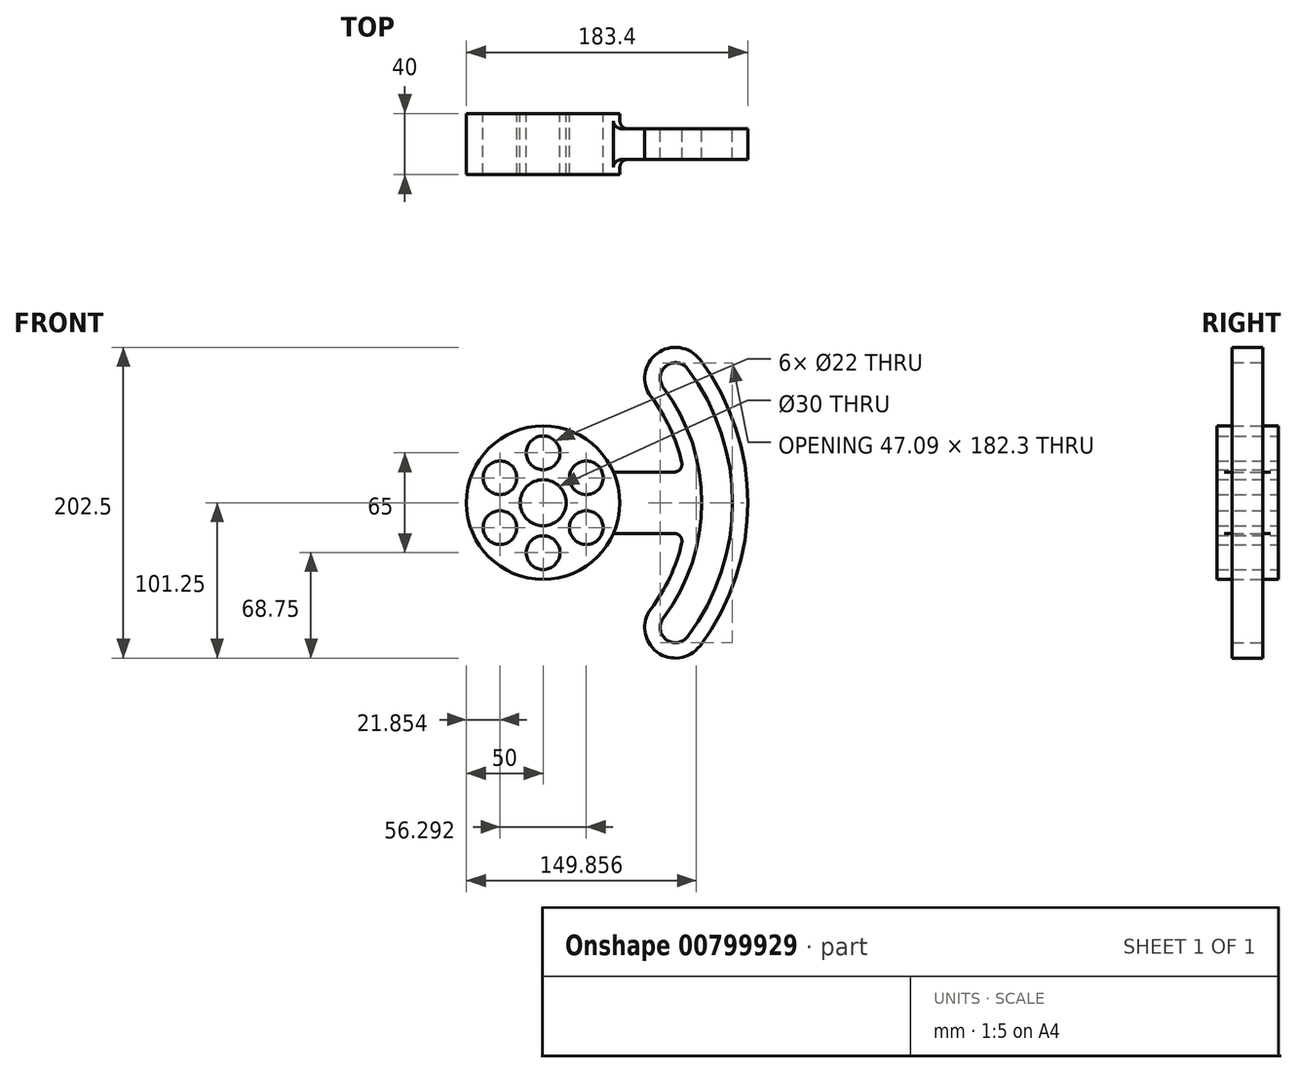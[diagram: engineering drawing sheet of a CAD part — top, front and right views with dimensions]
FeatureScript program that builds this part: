
annotation { "Feature Type Name" : "Feature", "Feature Type Description" : "" }
export const myFeature = defineFeature(function(context is Context, id is Id, definition is map)
    precondition{}
    {
        {
            var Q0;
            Q0=qCreatedBy(makeId("Front.planeOp"),FACE);
            var sketch = newSketch(context, id + "F0", { "sketchPlane" : qUnion([Q0])});
            skCircle(sketch, "E0", {"center": v(0, 0) * mm, "radius": 50 * mm});
            skCircle(sketch, "E1", {"center": v(0, 0) * mm, "radius": 15 * mm});
            skCircle(sketch, "E2", {"center": v(0, 0) * mm, "radius": 32.5 * mm, "construction": true});
            skCircle(sketch, "E3", {"center": v(0, 32.5) * mm, "radius": 11 * mm});
            skPoint(sketch, "E4.center", {"position": v(-21.6, 0) * mm});
            skCircle(sketch, "E5.1.0", {"center": v(-28.15, 16.25) * mm, "radius": 11 * mm});
            skCircle(sketch, "E5.2.0", {"center": v(-28.15, -16.25) * mm, "radius": 11 * mm});
            skCircle(sketch, "E5.3.0", {"center": v(0, -32.5) * mm, "radius": 11 * mm});
            skCircle(sketch, "E5.4.0", {"center": v(28.15, -16.25) * mm, "radius": 11 * mm});
            skCircle(sketch, "E5.5.0", {"center": v(28.15, 16.25) * mm, "radius": 11 * mm});
            skArc(sketch, "E6", {"start": v(70.24, -69.2) * mm, "mid": v(83.86, -45.87) * mm, "end": v(91.65, -20) * mm});
            skArc(sketch, "E7.0", {"start": v(78.23, -75.23) * mm, "mid": v(103.4, 0) * mm, "end": v(78.23, 75.23) * mm});
            skArc(sketch, "E8.0", {"start": v(94.2, -87.26) * mm, "mid": v(123.4, 0) * mm, "end": v(94.2, 87.26) * mm});
            skArc(sketch, "E9.0", {"start": v(102.19, -93.28) * mm, "mid": v(133.4, 0) * mm, "end": v(102.19, 93.28) * mm});
            skArc(sketch, "E10", {"start": v(102.19, 93.28) * mm, "mid": v(74.18, 97.22) * mm, "end": v(70.24, 69.2) * mm});
            skArc(sketch, "E11", {"start": v(70.24, -69.2) * mm, "mid": v(74.18, -97.22) * mm, "end": v(102.19, -93.28) * mm});
            skArc(sketch, "E12", {"start": v(94.2, 87.26) * mm, "mid": v(80.2, 89.23) * mm, "end": v(78.23, 75.23) * mm});
            skArc(sketch, "E13", {"start": v(78.23, -75.23) * mm, "mid": v(80.2, -89.23) * mm, "end": v(94.2, -87.26) * mm});
            skLineSegment(sketch, "E14", {"start": v(102.19, 93.28) * mm, "end": v(-21.6, 0) * mm, "construction": true});
            skLineSegment(sketch, "E15", {"start": v(102.19, -93.28) * mm, "end": v(-21.6, 0) * mm, "construction": true});
            skLineSegment(sketch, "E16", {"start": v(-21.6, 0) * mm, "end": v(188.18, 0) * mm, "construction": true});
            skPoint(sketch, "E16.endSnap0", {"position": v(123.4, 0) * mm});
            skPoint(sketch, "E17", {"position": v(93.4, 0) * mm});
            skPoint(sketch, "E18", {"position": v(50, 0) * mm});
            skLineSegment(sketch, "E19.bottom", {"start": v(45.83, 20) * mm, "end": v(91.65, 20) * mm});
            skLineSegment(sketch, "E19.top", {"start": v(45.83, -20) * mm, "end": v(91.65, -20) * mm});
            skArc(sketch, "E20.trimOffspring", {"start": v(91.65, 20) * mm, "mid": v(83.86, 45.87) * mm, "end": v(70.24, 69.2) * mm});
            skLineSegment(sketch, "E21", {"start": v(211.07, 41.65) * mm, "end": v(229.03, 36.04) * mm});
            skSolve(sketch);
        }
        {
            var Q0;
            Q0=makeQuery(id+"F0.imprint","IMPRINT",FACE,{"disambiguationData":[TD([[makeQuery(id+"F0.imprint","IMPRINT",EDGE,{"derivedFrom":sQuery(id+"F0.wireOp",EDGE,"E1")}),-1.0]])]});
            extrude(context, id + "F1", {"entities" : qUnion([Q0]), "endBound" : BoundingType.SYMMETRIC, "depth" : 40 * mm, "offsetDistance" : 25.4 * mm});
        }
        {
            var Q0;
            Q0 = qSketchRegion(id + "F0", true);
            extrude(context, id + "F2", {"entities" : qUnion([Q0]), "operationType" : NewBodyOperationType.ADD, "endBound" : BoundingType.SYMMETRIC, "depth" : 20 * mm, "offsetDistance" : 25.4 * mm});
        }
        {
            var Q0;
            Q0=makeQuery(id+"F2.opExtrude","SWEPT_EDGE",EDGE,{"disambiguationData":[OSD([sQuery(id+"F0.wireOp",EDGE,"E0"),sQuery(id+"F0.wireOp",EDGE,"E19.bottom")])]});
            var Q1;
            {var subQ0=sQuery(id+"F0.wireOp",EDGE,"E0");Q1=makeQuery(id+"F2.boolean.opBoolean","INTERSECT",EDGE,{"derivedFrom":[makeQuery(id+"F1.opExtrude","SWEPT_FACE",FACE,{"disambiguationData":[OSD([subQ0])]}),makeQuery(id+"F2.opExtrude","CAP_FACE",FACE,{"disambiguationData":[OSD([subQ0,sQuery(id+"F0.wireOp",EDGE,"E1"),sQuery(id+"F0.wireOp",EDGE,"E3"),sQuery(id+"F0.wireOp",EDGE,"E5.1.0"),sQuery(id+"F0.wireOp",EDGE,"E5.2.0"),sQuery(id+"F0.wireOp",EDGE,"E5.3.0"),sQuery(id+"F0.wireOp",EDGE,"E5.4.0"),sQuery(id+"F0.wireOp",EDGE,"E5.5.0"),sQuery(id+"F0.wireOp",EDGE,"E6"),sQuery(id+"F0.wireOp",EDGE,"E7.0"),sQuery(id+"F0.wireOp",EDGE,"E8.0"),sQuery(id+"F0.wireOp",EDGE,"E9.0"),sQuery(id+"F0.wireOp",EDGE,"E10"),sQuery(id+"F0.wireOp",EDGE,"E11"),sQuery(id+"F0.wireOp",EDGE,"E12"),sQuery(id+"F0.wireOp",EDGE,"E13"),sQuery(id+"F0.wireOp",EDGE,"E19.bottom"),sQuery(id+"F0.wireOp",EDGE,"E19.top"),sQuery(id+"F0.wireOp",EDGE,"E20.trimOffspring")])],"isStart":false})]});}
            var Q2;
            Q2=makeQuery(id+"F2.opExtrude","SWEPT_EDGE",EDGE,{"disambiguationData":[OSD([sQuery(id+"F0.wireOp",EDGE,"E0"),sQuery(id+"F0.wireOp",EDGE,"E19.top")])]});
            var Q3;
            {var subQ0=sQuery(id+"F0.wireOp",EDGE,"E0");Q3=makeQuery(id+"F2.boolean.opBoolean","INTERSECT",EDGE,{"derivedFrom":[makeQuery(id+"F1.opExtrude","SWEPT_FACE",FACE,{"disambiguationData":[OSD([subQ0])]}),makeQuery(id+"F2.opExtrude","CAP_FACE",FACE,{"disambiguationData":[OSD([subQ0,sQuery(id+"F0.wireOp",EDGE,"E1"),sQuery(id+"F0.wireOp",EDGE,"E3"),sQuery(id+"F0.wireOp",EDGE,"E5.1.0"),sQuery(id+"F0.wireOp",EDGE,"E5.2.0"),sQuery(id+"F0.wireOp",EDGE,"E5.3.0"),sQuery(id+"F0.wireOp",EDGE,"E5.4.0"),sQuery(id+"F0.wireOp",EDGE,"E5.5.0"),sQuery(id+"F0.wireOp",EDGE,"E6"),sQuery(id+"F0.wireOp",EDGE,"E7.0"),sQuery(id+"F0.wireOp",EDGE,"E8.0"),sQuery(id+"F0.wireOp",EDGE,"E9.0"),sQuery(id+"F0.wireOp",EDGE,"E10"),sQuery(id+"F0.wireOp",EDGE,"E11"),sQuery(id+"F0.wireOp",EDGE,"E12"),sQuery(id+"F0.wireOp",EDGE,"E13"),sQuery(id+"F0.wireOp",EDGE,"E19.bottom"),sQuery(id+"F0.wireOp",EDGE,"E19.top"),sQuery(id+"F0.wireOp",EDGE,"E20.trimOffspring")])],"isStart":true})]});}
            var Q4;
            Q4=makeQuery(id+"F2.opExtrude","SWEPT_EDGE",EDGE,{"disambiguationData":[OSD([sQuery(id+"F0.wireOp",EDGE,"E6"),sQuery(id+"F0.wireOp",EDGE,"E19.top")])]});
            var Q5;
            Q5=makeQuery(id+"F2.opExtrude","SWEPT_EDGE",EDGE,{"disambiguationData":[OSD([sQuery(id+"F0.wireOp",EDGE,"E19.bottom"),sQuery(id+"F0.wireOp",EDGE,"E20.trimOffspring")])]});
            fillet(context, id + "F3", {"entities" : qUnion([Q0, Q1, Q2, Q3, Q4, Q5]), "radius" : 5.08 * mm, "tangentPropagation" : true, "allowEdgeOverflow" : false});
        }
    });
